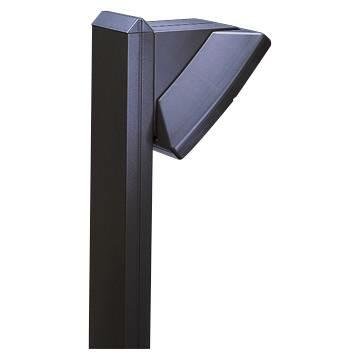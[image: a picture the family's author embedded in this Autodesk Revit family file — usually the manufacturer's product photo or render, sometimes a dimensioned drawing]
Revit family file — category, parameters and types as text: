
# Revit family: Lighting-ArredoUrbano-GEWISS-EXTRO-COLONNA_SINGOLA
name_source: partatom
category: Apparecchi per illuminazione
units: mm (PartAtom-declared; Revit-internal decimal feet)

## family parameters
Basato su piano di lavoro = Sì
Condiviso = No
Numero OmniClass = 23.80.00.00
Punto di calcolo locali = Sì
Quota connettore circolare = Usa diametro
Sempre verticale = Sì
Sorgente d'illuminazione = No
Taglio con vuoti quando caricato = No
Tipo di parte = Normale
Titolo OmniClass = Electric Power and Lighting

## types (1)
- GW82292 - COLONNA EXTRO SING.H.1300 G.GRAF.
    Altezza (mm) = 1300
    Altezza colonna = 1300 mm  [stored 4.26509 ft]
    Catalogo = LIGHTING
    Catalogo Serie = EXTRO
    Codice EAN = 8011564210387
    Codice Electrocod = 240
    Colonna = GEWISS - Grigio Graffite
    Colore = Grigio grafite
    Descrizione = COLONNA EXTRO SINGOLA H.1300 GRIGIO
    IDF = 5ea1d29d-4a77-4272-a550-a0c299649d89
    IDT = edb79119-9e68-4dab-b5a6-da154a75fe80
    Immagine tipo = GW82259.jpg
    Interramento (m) = 0.25
    Interramento consigliato = 250MM
    Larghezza colonna = 60 mm  [stored 0.19685 ft]
    Lunghezza colonna = 140 mm  [stored 0.459318 ft]
    Materiale = Alluminio estruso
    Modello = GW82292
    Produttore = GEWISS S.p.A.
    Prospetto di default = 1219 mm
    SEO = Colonna
    Scheda Tecnica = https://www.gewiss.com
    Tappo colonna = <Per categoria>
    URL = https://www.gewiss.com
    Versione file RFA = 20.11

note: [stored X ft] marks values corroborated as IEEE doubles in the binary element streams (Revit-internal decimal feet)
